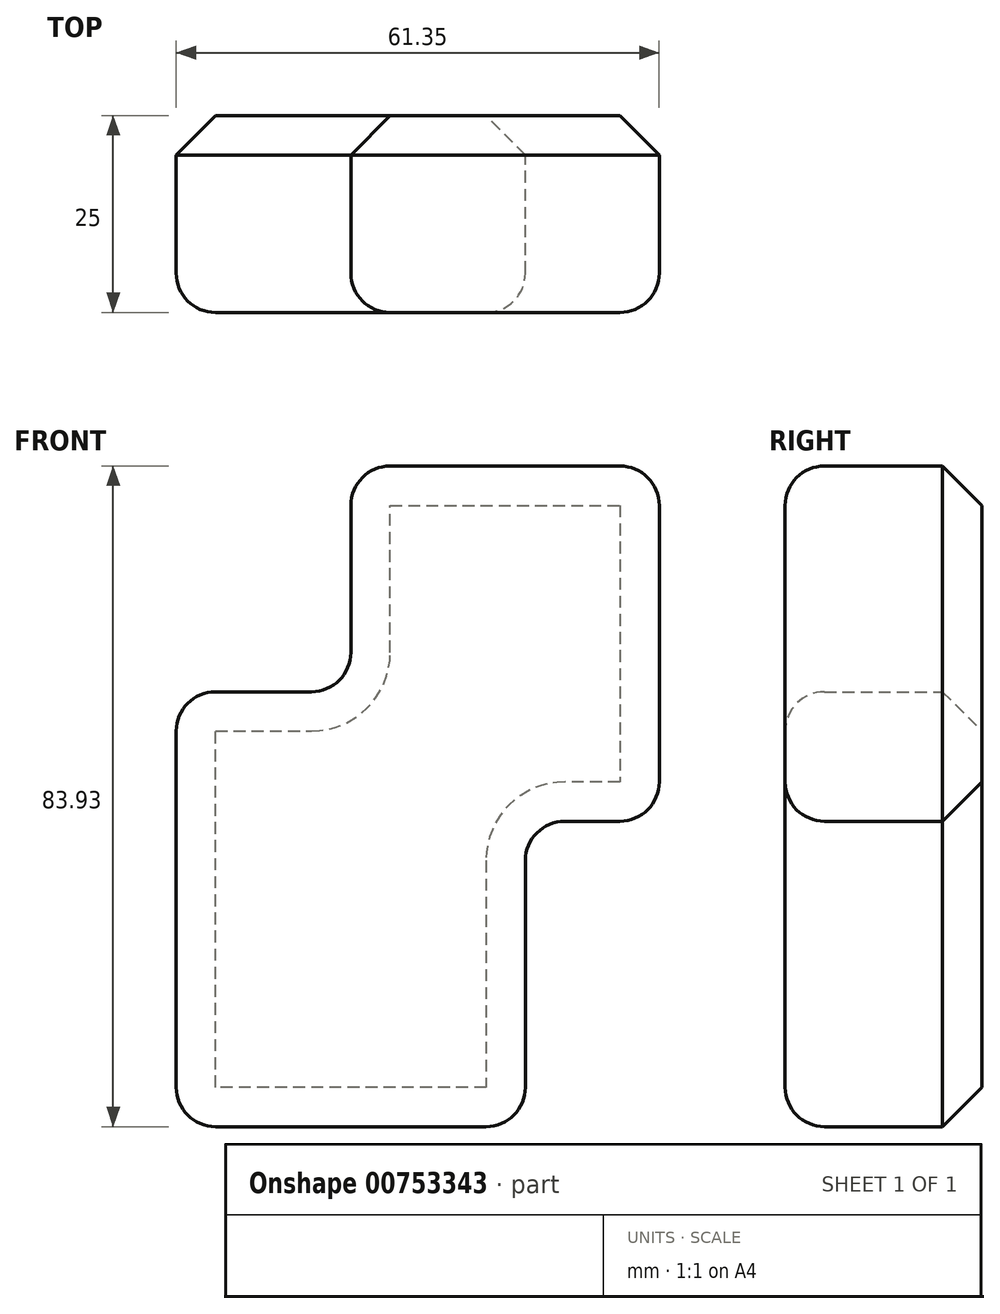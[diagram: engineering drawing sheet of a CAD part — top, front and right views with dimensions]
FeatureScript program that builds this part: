
annotation { "Feature Type Name" : "Feature", "Feature Type Description" : "" }
export const myFeature = defineFeature(function(context is Context, id is Id, definition is map)
    precondition{}
    {
        {
            var Q0;
            Q0=qCreatedBy(makeId("Front.planeOp"),FACE);
            var sketch = newSketch(context, id + "F0", { "sketchPlane" : qUnion([Q0])});
            skLineSegment(sketch, "E0.bottom", {"start": v(-16.32, 16.45) * mm, "end": v(-4.14, 16.45) * mm});
            skLineSegment(sketch, "E0.top", {"start": v(-16.32, -38.8) * mm, "end": v(18.04, -38.8) * mm});
            skLineSegment(sketch, "E0.left", {"start": v(-21.32, 11.45) * mm, "end": v(-21.32, -33.8) * mm});
            skLineSegment(sketch, "E0.right", {"start": v(23.04, -5) * mm, "end": v(23.04, -33.8) * mm});
            skPoint(sketch, "E1.firstSnap0", {"position": v(0.86, 16.45) * mm});
            skLineSegment(sketch, "E1.bottom", {"start": v(5.86, 45.13) * mm, "end": v(35.03, 45.13) * mm});
            skLineSegment(sketch, "E1.top", {"start": v(28.04, 0) * mm, "end": v(35.03, 0) * mm});
            skLineSegment(sketch, "E1.left", {"start": v(0.86, 40.13) * mm, "end": v(0.86, 21.45) * mm});
            skLineSegment(sketch, "E1.right", {"start": v(40.03, 40.13) * mm, "end": v(40.03, 5) * mm});
            skPoint(sketch, "E2.orphan", {"position": v(23.04, 16.45) * mm});
            skArc(sketch, "E3.filletArc", {"start": v(-4.14, 16.45) * mm, "mid": v(-0.6, 17.91) * mm, "end": v(0.86, 21.45) * mm});
            skPoint(sketch, "E4.visualSharp", {"position": v(23.04, 0) * mm});
            skArc(sketch, "E4.filletArc", {"start": v(28.04, 0) * mm, "mid": v(24.5, -1.46) * mm, "end": v(23.04, -5) * mm});
            skPoint(sketch, "E5.visualSharp", {"position": v(-21.32, 16.45) * mm});
            skArc(sketch, "E5.filletArc", {"start": v(-16.32, 16.45) * mm, "mid": v(-19.86, 14.98) * mm, "end": v(-21.32, 11.45) * mm});
            skPoint(sketch, "E6.visualSharp", {"position": v(0.86, 45.13) * mm});
            skArc(sketch, "E6.filletArc", {"start": v(5.86, 45.13) * mm, "mid": v(2.32, 43.66) * mm, "end": v(0.86, 40.13) * mm});
            skPoint(sketch, "E7.visualSharp", {"position": v(40.03, 0) * mm});
            skArc(sketch, "E7.filletArc", {"start": v(35.03, 0) * mm, "mid": v(38.57, 1.46) * mm, "end": v(40.03, 5) * mm});
            skPoint(sketch, "E8.visualSharp", {"position": v(23.04, -38.8) * mm});
            skArc(sketch, "E8.filletArc", {"start": v(18.04, -38.8) * mm, "mid": v(21.57, -37.33) * mm, "end": v(23.04, -33.8) * mm});
            skPoint(sketch, "E9.visualSharp", {"position": v(40.03, 45.13) * mm});
            skArc(sketch, "E9.filletArc", {"start": v(40.03, 40.13) * mm, "mid": v(38.57, 43.66) * mm, "end": v(35.03, 45.13) * mm});
            skPoint(sketch, "E10.visualSharp", {"position": v(-21.32, -38.8) * mm});
            skArc(sketch, "E10.filletArc", {"start": v(-21.32, -33.8) * mm, "mid": v(-19.86, -37.33) * mm, "end": v(-16.32, -38.8) * mm});
            skSolve(sketch);
        }
        {
            var Q0;
            Q0=makeQuery(id+"F0.imprint","IMPRINT",FACE,{"disambiguationData":[TD([[makeQuery(id+"F0.imprint","IMPRINT",EDGE,{"derivedFrom":sQuery(id+"F0.wireOp",EDGE,"E0.bottom")}),-1.0]])]});
            extrude(context, id + "F1", {"entities" : qUnion([Q0]), "depth" : 25 * mm, "offsetDistance" : 25 * mm});
        }
        {
            var Q0;
            Q0=makeQuery(id+"F1.opExtrude","CAP_EDGE",EDGE,{"disambiguationData":[OSD([sQuery(id+"F0.wireOp",EDGE,"E0.top")])],"isStart":false});
            fillet(context, id + "F2", {"entities" : qUnion([Q0]), "radius" : 5 * mm, "tangentPropagation" : true, "allowEdgeOverflow" : false});
        }
        {
            var Q0;
            Q0=makeQuery(id+"F1.opExtrude","CAP_FACE",FACE,{"disambiguationData":[OSD([sQuery(id+"F0.wireOp",EDGE,"E0.bottom"),sQuery(id+"F0.wireOp",EDGE,"E0.top"),sQuery(id+"F0.wireOp",EDGE,"E0.left"),sQuery(id+"F0.wireOp",EDGE,"E0.right"),sQuery(id+"F0.wireOp",EDGE,"E1.bottom"),sQuery(id+"F0.wireOp",EDGE,"E1.top"),sQuery(id+"F0.wireOp",EDGE,"E1.left"),sQuery(id+"F0.wireOp",EDGE,"E1.right"),sQuery(id+"F0.wireOp",EDGE,"E3.filletArc"),sQuery(id+"F0.wireOp",EDGE,"E4.filletArc"),sQuery(id+"F0.wireOp",EDGE,"E5.filletArc"),sQuery(id+"F0.wireOp",EDGE,"E6.filletArc"),sQuery(id+"F0.wireOp",EDGE,"E7.filletArc"),sQuery(id+"F0.wireOp",EDGE,"E8.filletArc"),sQuery(id+"F0.wireOp",EDGE,"E9.filletArc"),sQuery(id+"F0.wireOp",EDGE,"E10.filletArc")])],"isStart":true});
            chamfer(context, id + "F3", {"entities" : qUnion([Q0]), "width" : 5 * mm, "tangentPropagation" : true});
        }
    });
